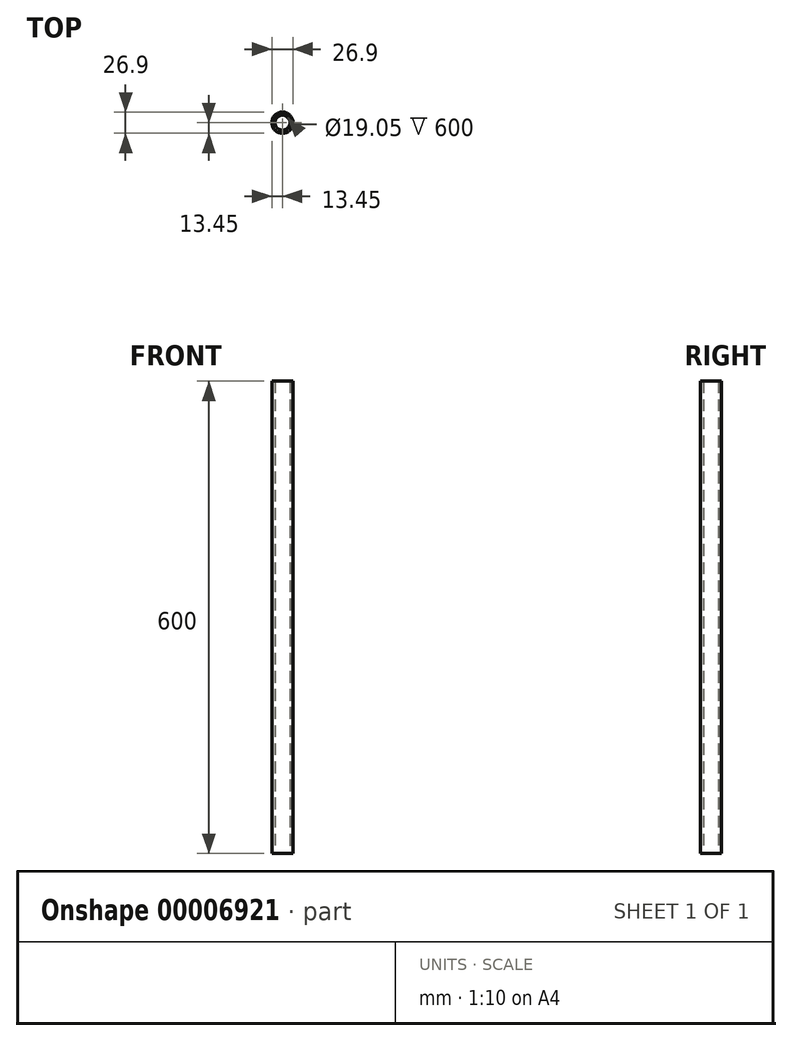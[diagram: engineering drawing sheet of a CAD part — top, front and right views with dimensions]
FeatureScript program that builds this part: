
annotation { "Feature Type Name" : "Feature", "Feature Type Description" : "" }
export const myFeature = defineFeature(function(context is Context, id is Id, definition is map)
    precondition{}
    {
        {
            var Q0;
            Q0=qCreatedBy(makeId("Top.planeOp"),FACE);
            var sketch = newSketch(context, id + "F0", { "sketchPlane" : qUnion([Q0])});
            skCircle(sketch, "E0", {"center": v(0, 0) * mm, "radius": 13.45 * mm});
            skCircle(sketch, "E1", {"center": v(0, 0) * mm, "radius": 9.53 * mm});
            skSolve(sketch);
        }
        {
            var Q0;
            Q0=makeQuery(id+"F0.imprint","IMPRINT",FACE,{"disambiguationData":[TD([[makeQuery(id+"F0.imprint","IMPRINT",EDGE,{"derivedFrom":sQuery(id+"F0.wireOp",EDGE,"E0")}),1.0]])]});
            extrude(context, id + "F1", {"entities" : qUnion([Q0]), "depth" : (600) * mm});
        }
    });
